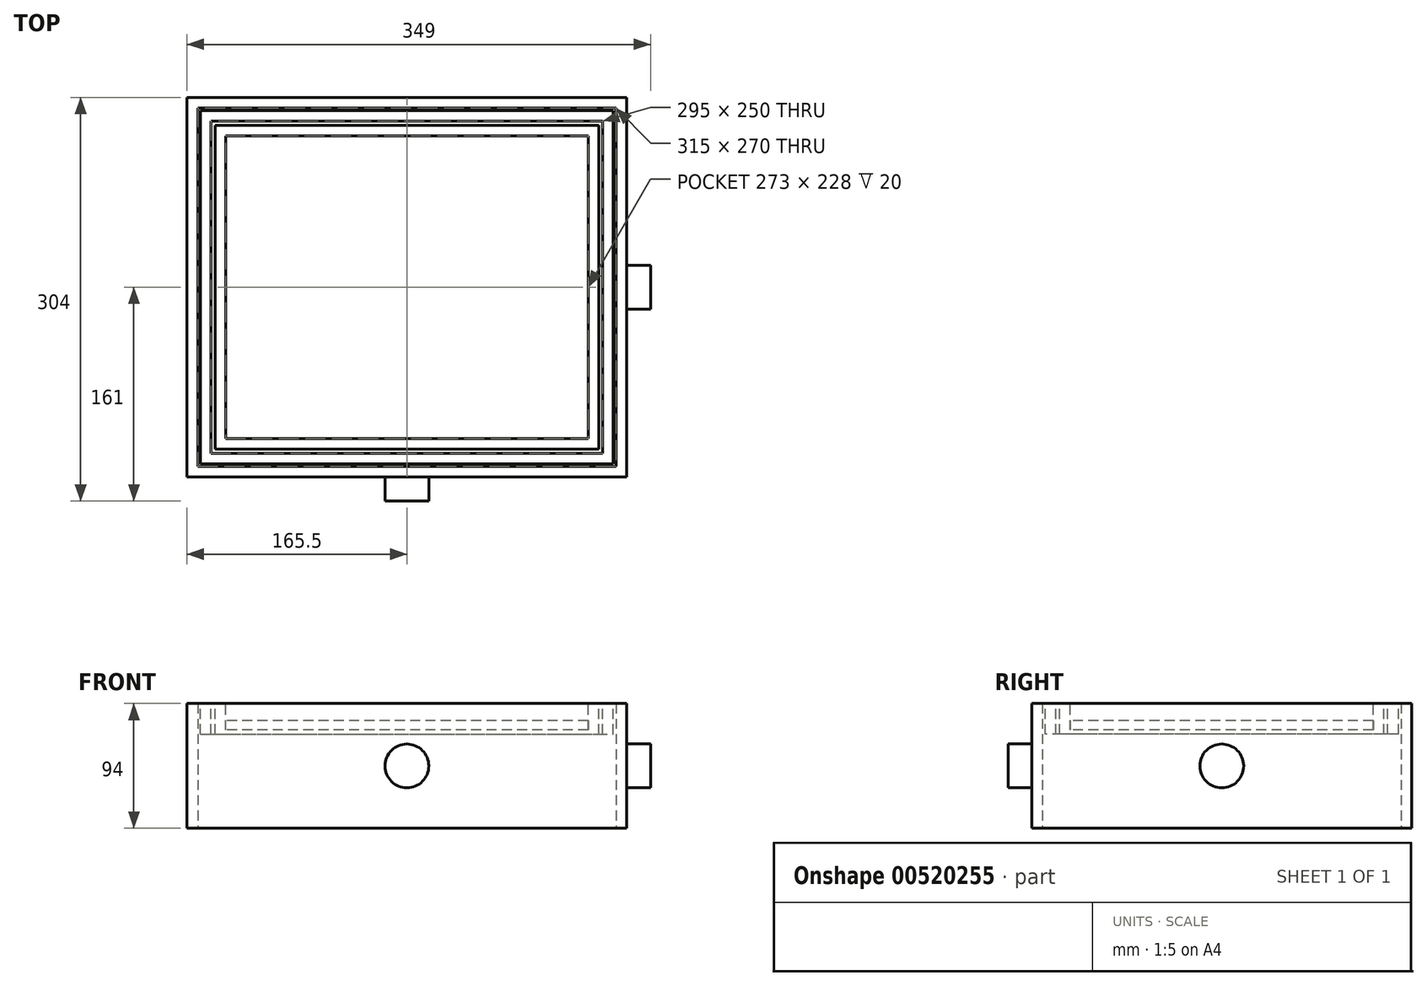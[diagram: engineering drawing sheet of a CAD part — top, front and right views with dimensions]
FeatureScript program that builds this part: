
annotation { "Feature Type Name" : "Feature", "Feature Type Description" : "" }
export const myFeature = defineFeature(function(context is Context, id is Id, definition is map)
    precondition{}
    {
        {
            var Q0;
            Q0=qCreatedBy(makeId("Top.planeOp"),FACE);
            var sketch = newSketch(context, id + "F0", { "sketchPlane" : qUnion([Q0])});
            skLineSegment(sketch, "E0.bottom", {"start": v(165.5, 143) * mm, "end": v(-165.5, 143) * mm});
            skLineSegment(sketch, "E0.top", {"start": v(165.5, -143) * mm, "end": v(-165.5, -143) * mm});
            skLineSegment(sketch, "E0.left", {"start": v(165.5, 143) * mm, "end": v(165.5, -143) * mm});
            skLineSegment(sketch, "E0.right", {"start": v(-165.5, 143) * mm, "end": v(-165.5, -143) * mm});
            skPoint(sketch, "E0.middle", {"position": v(0, 0) * mm});
            skLineSegment(sketch, "E1.0", {"start": v(157.5, -135) * mm, "end": v(-157.5, -135) * mm});
            skLineSegment(sketch, "E1.1", {"start": v(157.5, 135) * mm, "end": v(157.5, -135) * mm});
            skLineSegment(sketch, "E1.2", {"start": v(157.5, 135) * mm, "end": v(-157.5, 135) * mm});
            skLineSegment(sketch, "E1.3", {"start": v(-157.5, 135) * mm, "end": v(-157.5, -135) * mm});
            skSolve(sketch);
        }
        {
            var Q0;
            Q0=makeQuery(id+"F0.imprint","IMPRINT",FACE,{"disambiguationData":[TD([[makeQuery(id+"F0.imprint","IMPRINT",EDGE,{"derivedFrom":sQuery(id+"F0.wireOp",EDGE,"E0.bottom")}),1.0]])]});
            extrude(context, id + "F1", {"entities" : qUnion([Q0]), "depth" : 94 * mm, "offsetDistance" : 25.4 * mm});
        }
        {
            var Q0;
            Q0=makeQuery(id+"F1.opExtrude","SWEPT_FACE",FACE,{"disambiguationData":[OSD([sQuery(id+"F0.wireOp",EDGE,"E0.left")])]});
            var sketch = newSketch(context, id + "F2", { "sketchPlane" : qUnion([Q0])});
            skCircle(sketch, "E2", {"center": v(0, 47) * mm, "radius": 16.5 * mm});
            skLineSegment(sketch, "E3", {"start": v(0, 47) * mm, "end": v(0, 94) * mm, "construction": true});
            skLineSegment(sketch, "E4", {"start": v(0, 47) * mm, "end": v(0, 0) * mm, "construction": true});
            skLineSegment(sketch, "E5", {"start": v(-143, 47) * mm, "end": v(0, 47) * mm, "construction": true});
            skLineSegment(sketch, "E6", {"start": v(0, 47) * mm, "end": v(143, 47) * mm, "construction": true});
            skSolve(sketch);
        }
        {
            var Q0;
            Q0=makeQuery(id+"F2.imprint","IMPRINT",FACE,{"disambiguationData":[TD([[makeQuery(id+"F2.imprint","IMPRINT",EDGE,{"derivedFrom":sQuery(id+"F2.wireOp",EDGE,"E2")}),1.0]])]});
            extrude(context, id + "F3", {"entities" : qUnion([Q0]), "operationType" : NewBodyOperationType.ADD, "depth" : 18 * mm, "offsetDistance" : 25.4 * mm});
        }
        {
            var Q0;
            Q0=makeQuery(id+"F1.opExtrude","SWEPT_FACE",FACE,{"disambiguationData":[OSD([sQuery(id+"F0.wireOp",EDGE,"E0.top")])]});
            var sketch = newSketch(context, id + "F4", { "sketchPlane" : qUnion([Q0])});
            skCircle(sketch, "E7", {"center": v(0, 47) * mm, "radius": 16.5 * mm});
            skPoint(sketch, "E7.centerSnap0", {"position": v(0, 0) * mm});
            skLineSegment(sketch, "E8", {"start": v(0, 47) * mm, "end": v(0, 0) * mm, "construction": true});
            skLineSegment(sketch, "E9", {"start": v(0, 47) * mm, "end": v(0, 94) * mm, "construction": true});
            skLineSegment(sketch, "E10", {"start": v(0, 47) * mm, "end": v(165.5, 47) * mm, "construction": true});
            skLineSegment(sketch, "E11", {"start": v(0, 47) * mm, "end": v(-165.5, 47) * mm, "construction": true});
            skSolve(sketch);
        }
        {
            var Q0;
            Q0=makeQuery(id+"F4.imprint","IMPRINT",FACE,{"disambiguationData":[TD([[makeQuery(id+"F4.imprint","IMPRINT",EDGE,{"derivedFrom":sQuery(id+"F4.wireOp",EDGE,"E7")}),1.0]])]});
            extrude(context, id + "F5", {"entities" : qUnion([Q0]), "operationType" : NewBodyOperationType.ADD, "depth" : 18 * mm, "offsetDistance" : 25.4 * mm});
        }
        {
            var Q0;
            Q0=makeQuery(id+"F1.opExtrude","CAP_FACE",FACE,{"disambiguationData":[OSD([sQuery(id+"F0.wireOp",EDGE,"E0.bottom"),sQuery(id+"F0.wireOp",EDGE,"E0.top"),sQuery(id+"F0.wireOp",EDGE,"E0.left"),sQuery(id+"F0.wireOp",EDGE,"E0.right"),sQuery(id+"F0.wireOp",EDGE,"E1.0"),sQuery(id+"F0.wireOp",EDGE,"E1.1"),sQuery(id+"F0.wireOp",EDGE,"E1.2"),sQuery(id+"F0.wireOp",EDGE,"E1.3")])],"isStart":false});
            var sketch = newSketch(context, id + "F6", { "sketchPlane" : qUnion([Q0])});
            skLineSegment(sketch, "E12.bottom", {"start": v(-144.5, 122) * mm, "end": v(144.5, 122) * mm});
            skLineSegment(sketch, "E12.top", {"start": v(-144.5, -122) * mm, "end": v(144.5, -122) * mm});
            skLineSegment(sketch, "E12.left", {"start": v(-144.5, 122) * mm, "end": v(-144.5, -122) * mm});
            skLineSegment(sketch, "E12.right", {"start": v(144.5, 122) * mm, "end": v(144.5, -122) * mm});
            skPoint(sketch, "E12.middle", {"position": v(0, 0) * mm});
            skLineSegment(sketch, "E13.bottom", {"start": v(-147.5, 125) * mm, "end": v(147.5, 125) * mm});
            skLineSegment(sketch, "E13.top", {"start": v(-147.5, -125) * mm, "end": v(147.5, -125) * mm});
            skLineSegment(sketch, "E13.left", {"start": v(-147.5, 125) * mm, "end": v(-147.5, -125) * mm});
            skLineSegment(sketch, "E13.right", {"start": v(147.5, 125) * mm, "end": v(147.5, -125) * mm});
            skLineSegment(sketch, "E14.bottom", {"start": v(-155.5, 133) * mm, "end": v(155.5, 133) * mm});
            skLineSegment(sketch, "E14.top", {"start": v(-155.5, -133) * mm, "end": v(155.5, -133) * mm});
            skLineSegment(sketch, "E14.left", {"start": v(-155.5, 133) * mm, "end": v(-155.5, -133) * mm});
            skLineSegment(sketch, "E14.right", {"start": v(155.5, 133) * mm, "end": v(155.5, -133) * mm});
            skLineSegment(sketch, "E15.bottom", {"start": v(-136.5, 114) * mm, "end": v(136.5, 114) * mm});
            skLineSegment(sketch, "E15.top", {"start": v(-136.5, -114) * mm, "end": v(136.5, -114) * mm});
            skLineSegment(sketch, "E15.left", {"start": v(-136.5, 114) * mm, "end": v(-136.5, -114) * mm});
            skLineSegment(sketch, "E15.right", {"start": v(136.5, 114) * mm, "end": v(136.5, -114) * mm});
            skSolve(sketch);
        }
        {
            var Q0;
            Q0=makeQuery(id+"F6.imprint","IMPRINT",FACE,{"disambiguationData":[TD([[makeQuery(id+"F6.imprint","IMPRINT",EDGE,{"derivedFrom":sQuery(id+"F6.wireOp",EDGE,"E13.bottom")}),1.0]])]});
            var Q1;
            Q1=makeQuery(id+"F6.imprint","IMPRINT",FACE,{"disambiguationData":[TD([[makeQuery(id+"F6.imprint","IMPRINT",EDGE,{"derivedFrom":sQuery(id+"F6.wireOp",EDGE,"E12.bottom")}),-1.0]])]});
            extrude(context, id + "F7", {"entities" : qUnion([Q0, Q1]), "oppositeDirection" : true, "depth" : 23 * mm, "offsetDistance" : 25 * mm});
        }
        {
            var Q0;
            Q0=makeQuery(id+"F7.opExtrude","SWEPT_FACE",FACE,{"disambiguationData":[OSD([sQuery(id+"F6.wireOp",EDGE,"E15.left")])]});
            var sketch = newSketch(context, id + "F8", { "sketchPlane" : qUnion([Q0])});
            skLineSegment(sketch, "E16.bottom", {"start": v(-114, 74) * mm, "end": v(114, 74) * mm});
            skLineSegment(sketch, "E16.top", {"start": v(-114, 71) * mm, "end": v(114, 71) * mm});
            skLineSegment(sketch, "E16.left", {"start": v(-114, 74) * mm, "end": v(-114, 71) * mm});
            skLineSegment(sketch, "E16.right", {"start": v(114, 74) * mm, "end": v(114, 71) * mm});
            skSolve(sketch);
        }
        {
            var Q0;
            Q0=makeQuery(id+"F8.imprint","IMPRINT",FACE,{"disambiguationData":[TD([[makeQuery(id+"F8.imprint","IMPRINT",EDGE,{"derivedFrom":sQuery(id+"F8.wireOp",EDGE,"E16.bottom")}),-1.0]])]});
            extrude(context, id + "F9", {"entities" : qUnion([Q0]), "operationType" : NewBodyOperationType.ADD, "endBound" : BoundingType.UP_TO_NEXT, "depth" : 25 * mm, "offsetDistance" : 25 * mm});
        }
        {
            var Q0;
            Q0=makeQuery(id+"F7.opExtrude","SWEPT_FACE",FACE,{"disambiguationData":[OSD([sQuery(id+"F6.wireOp",EDGE,"E15.left")])]});
            var sketch = newSketch(context, id + "F10", { "sketchPlane" : qUnion([Q0])});
            skLineSegment(sketch, "E17", {"start": v(-114, 81) * mm, "end": v(114, 81) * mm});
            skSolve(sketch);
        }
        {
            var Q0;
            {var subQ0=sQuery(id+"F10.wireOp",EDGE,"E17");Q0=makeQuery(id+"F10.imprint","IMPRINT",FACE,{"disambiguationData":[TD([[makeQuery(id+"F10.imprint","IMPRINT",EDGE,{"derivedFrom":subQ0}),-1.0]])]});}
            extrude(context, id + "F11", {"entities" : qUnion([Q0]), "endBound" : BoundingType.UP_TO_NEXT, "depth" : 25 * mm, "offsetDistance" : 25 * mm});
        }
    });
